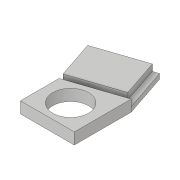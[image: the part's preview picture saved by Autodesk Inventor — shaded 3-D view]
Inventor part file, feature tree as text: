
AUTODESK INVENTOR PART (.ipt)
format: ipt  version: 2018.3 (Build 223284000, 284)  size: 113,664 bytes
history: native  units: in
note: dims shown in document units (in); Inventor stores cm internally (conversion verified against a paired STEP export)
features: extrude x3, sketch x3
ambient origin geometry x8: Origin, YZ Plane, XZ Plane, XY Plane, X Axis, Y Axis, Z Axis, Center Point
bodies: Solid1 (feature_tree)
feature tree (6):
  extrude  "Extrusion1"  Depth=0.119in
  extrude  "Extrusion2"  Depth=0.1105in
  extrude  "Extrusion3"  Depth=0.125in
  sketch  "Sketch1"  dims[d0=0.75in d1=0.875in d2=1.1003in d3=1.0432in d4=0.6925in d5=0.221in d6=0.0in d11=0.119in]
  sketch  "Sketch2"  dims[d13=0.125in d14=0.0in d17=0.1105in]
  sketch  "Sketch3"  dims[d18=0.125in d19=0.0in d20=0.4509in d21=0.5216in]
